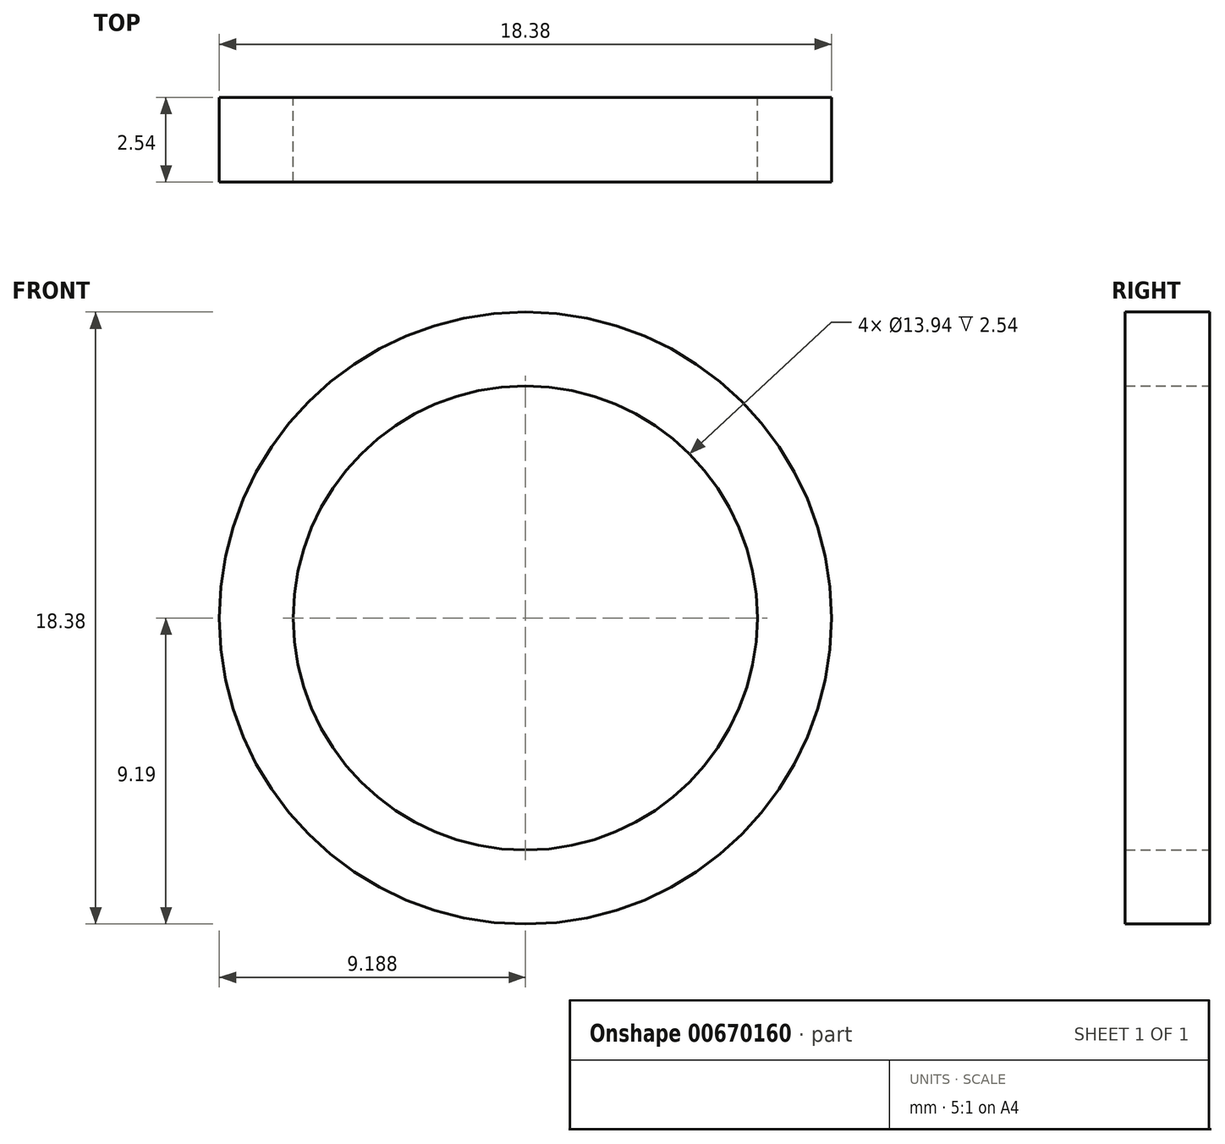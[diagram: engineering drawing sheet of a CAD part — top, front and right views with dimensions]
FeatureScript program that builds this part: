
annotation { "Feature Type Name" : "Feature", "Feature Type Description" : "" }
export const myFeature = defineFeature(function(context is Context, id is Id, definition is map)
    precondition{}
    {
        {
            var Q0;
            Q0=qCreatedBy(makeId("Front.planeOp"),FACE);
            var sketch = newSketch(context, id + "F0", { "sketchPlane" : qUnion([Q0])});
            skCircle(sketch, "E0", {"center": v(1.64, 0) * mm, "radius": 9.2 * mm});
            skCircle(sketch, "E1", {"center": v(1.64, 0) * mm, "radius": 6.97 * mm});
            skCircle(sketch, "E2", {"center": v(1.64, 0) * mm, "radius": 5.05 * mm});
            skCircle(sketch, "E3", {"center": v(1.64, 0) * mm, "radius": 2.94 * mm});
            skSolve(sketch);
        }
        {
            var Q0;
            Q0 = qSketchRegion(id + "F0", true);
            extrude(context, id + "F1", {"entities" : qUnion([Q0]), "depth" : 2.54 * mm, "offsetDistance" : 25.4 * mm});
        }
        {
            var Q0;
            Q0=makeQuery(id+"F1.opExtrude","SWEPT_BODY",BODY,{"disambiguationData":[OSD([sQuery(id+"F0.wireOp",EDGE,"E0"),sQuery(id+"F0.wireOp",EDGE,"E1")])]});
            var Q1;
            Q1=makeQuery(id+"F1.opExtrude","CAP_EDGE",EDGE,{"disambiguationData":[OSD([sQuery(id+"F0.wireOp",EDGE,"E1")])],"isStart":false});
            circularPattern(context, id + "F2", {"entities" : qUnion([Q0]), "axis" : qUnion([Q1]), "angle" : 360 * degree, "instanceCount" : 4, "equalSpace" : true});
        }
    });
